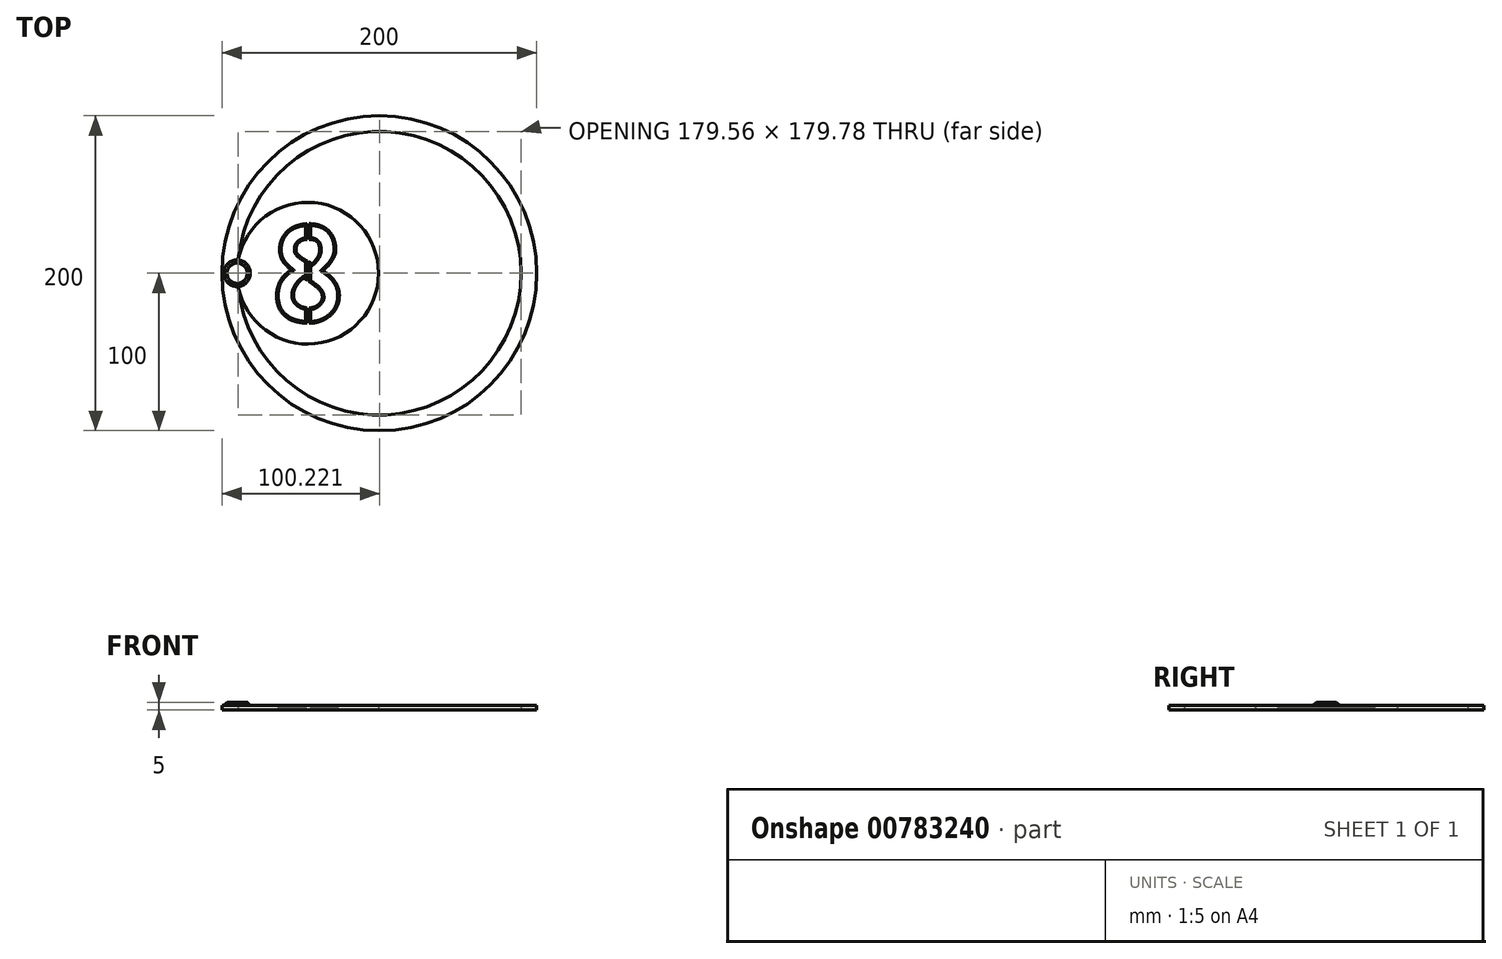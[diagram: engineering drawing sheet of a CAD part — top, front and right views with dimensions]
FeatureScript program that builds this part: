
annotation { "Feature Type Name" : "Feature", "Feature Type Description" : "" }
export const myFeature = defineFeature(function(context is Context, id is Id, definition is map)
    precondition{}
    {
        {
            var Q0;
            Q0=qCreatedBy(makeId("Top.planeOp"),FACE);
            var sketch = newSketch(context, id + "F0", { "sketchPlane" : qUnion([Q0])});
            skCircle(sketch, "E0", {"center": v(0, 0) * mm, "radius": 100 * mm});
            skArc(sketch, "E1", {"start": v(-89.56, -8.9) * mm, "mid": v(90, 0) * mm, "end": v(-89.56, 8.9) * mm});
            skArc(sketch, "E2", {"start": v(-89.56, -8.9) * mm, "mid": v(-0.45, 0) * mm, "end": v(-89.56, 8.9) * mm});
            skText(sketch, "E3", { "text": "8", "fontName": "AllertaStencil-Regular.ttf"});
            const initialGuessF0  = {"E3": [-0.07008, -0.03, 1, 0, 0.06]};
            skSetInitialGuess(sketch, initialGuessF0);
            skSolve(sketch);
        }
        {
            var Q0;
            Q0=makeQuery(id+"F0.imprint","IMPRINT",FACE,{"disambiguationData":[TD([[makeQuery(id+"F0.imprint","IMPRINT",EDGE,{"derivedFrom":sQuery(id+"F0.wireOp",EDGE,"E0")}),1.0]])]});
            extrude(context, id + "F1", {"entities" : qUnion([Q0]), "depth" : 3 * mm, "offsetDistance" : 25 * mm});
        }
        {
            var Q0;
            Q0=makeQuery(id+"F1.opExtrude","CAP_FACE",FACE,{"disambiguationData":[OSD([sQuery(id+"F0.wireOp",EDGE,"E0"),sQuery(id+"F0.wireOp",EDGE,"E1"),sQuery(id+"F0.wireOp",EDGE,"E2"),sQuery(id+"F0.wireOp",EDGE,"E3.sketch_text.stroke-0"),sQuery(id+"F0.wireOp",EDGE,"E3.sketch_text.stroke-1"),sQuery(id+"F0.wireOp",EDGE,"E3.sketch_text.stroke-2"),sQuery(id+"F0.wireOp",EDGE,"E3.sketch_text.stroke-3"),sQuery(id+"F0.wireOp",EDGE,"E3.sketch_text.stroke-4"),sQuery(id+"F0.wireOp",EDGE,"E3.sketch_text.stroke-5"),sQuery(id+"F0.wireOp",EDGE,"E3.sketch_text.stroke-6"),sQuery(id+"F0.wireOp",EDGE,"E3.sketch_text.stroke-7"),sQuery(id+"F0.wireOp",EDGE,"E3.sketch_text.stroke-8"),sQuery(id+"F0.wireOp",EDGE,"E3.sketch_text.stroke-9"),sQuery(id+"F0.wireOp",EDGE,"E3.sketch_text.stroke-10"),sQuery(id+"F0.wireOp",EDGE,"E3.sketch_text.stroke-11"),sQuery(id+"F0.wireOp",EDGE,"E3.sketch_text.stroke-12"),sQuery(id+"F0.wireOp",EDGE,"E3.sketch_text.stroke-13"),sQuery(id+"F0.wireOp",EDGE,"E3.sketch_text.stroke-14"),sQuery(id+"F0.wireOp",EDGE,"E3.sketch_text.stroke-15"),sQuery(id+"F0.wireOp",EDGE,"E3.sketch_text.stroke-16"),sQuery(id+"F0.wireOp",EDGE,"E3.sketch_text.stroke-17"),sQuery(id+"F0.wireOp",EDGE,"E3.sketch_text.stroke-18"),sQuery(id+"F0.wireOp",EDGE,"E3.sketch_text.stroke-19"),sQuery(id+"F0.wireOp",EDGE,"E3.sketch_text.stroke-20"),sQuery(id+"F0.wireOp",EDGE,"E3.sketch_text.stroke-21"),sQuery(id+"F0.wireOp",EDGE,"E3.sketch_text.stroke-22"),sQuery(id+"F0.wireOp",EDGE,"E3.sketch_text.stroke-23"),sQuery(id+"F0.wireOp",EDGE,"E3.sketch_text.stroke-24"),sQuery(id+"F0.wireOp",EDGE,"E3.sketch_text.stroke-25"),sQuery(id+"F0.wireOp",EDGE,"E3.sketch_text.stroke-26"),sQuery(id+"F0.wireOp",EDGE,"E3.sketch_text.stroke-27"),sQuery(id+"F0.wireOp",EDGE,"E3.sketch_text.stroke-28"),sQuery(id+"F0.wireOp",EDGE,"E3.sketch_text.stroke-29"),sQuery(id+"F0.wireOp",EDGE,"E3.sketch_text.stroke-30"),sQuery(id+"F0.wireOp",EDGE,"E3.sketch_text.stroke-31"),sQuery(id+"F0.wireOp",EDGE,"E3.sketch_text.stroke-32"),sQuery(id+"F0.wireOp",EDGE,"E3.sketch_text.stroke-33"),sQuery(id+"F0.wireOp",EDGE,"E3.sketch_text.stroke-34"),sQuery(id+"F0.wireOp",EDGE,"E3.sketch_text.stroke-35"),sQuery(id+"F0.wireOp",EDGE,"E3.sketch_text.stroke-36"),sQuery(id+"F0.wireOp",EDGE,"E3.sketch_text.stroke-37"),sQuery(id+"F0.wireOp",EDGE,"E3.sketch_text.stroke-38"),sQuery(id+"F0.wireOp",EDGE,"E3.sketch_text.stroke-39"),sQuery(id+"F0.wireOp",EDGE,"E3.sketch_text.stroke-40"),sQuery(id+"F0.wireOp",EDGE,"E3.sketch_text.stroke-41"),sQuery(id+"F0.wireOp",EDGE,"E3.sketch_text.stroke-42"),sQuery(id+"F0.wireOp",EDGE,"E3.sketch_text.stroke-43"),sQuery(id+"F0.wireOp",EDGE,"E3.sketch_text.stroke-44"),sQuery(id+"F0.wireOp",EDGE,"E3.sketch_text.stroke-45"),sQuery(id+"F0.wireOp",EDGE,"E3.sketch_text.stroke-46"),sQuery(id+"F0.wireOp",EDGE,"E3.sketch_text.stroke-47"),sQuery(id+"F0.wireOp",EDGE,"E3.sketch_text.stroke-48"),sQuery(id+"F0.wireOp",EDGE,"E3.sketch_text.stroke-49"),sQuery(id+"F0.wireOp",EDGE,"E3.sketch_text.stroke-50"),sQuery(id+"F0.wireOp",EDGE,"E3.sketch_text.stroke-51"),sQuery(id+"F0.wireOp",EDGE,"E3.sketch_text.stroke-52"),sQuery(id+"F0.wireOp",EDGE,"E3.sketch_text.stroke-53")])],"isStart":false});
            var sketch = newSketch(context, id + "F2", { "sketchPlane" : qUnion([Q0])});
            skCircle(sketch, "E4", {"center": v(-90.34, 0) * mm, "radius": 8.44 * mm});
            skSolve(sketch);
        }
        {
            var Q0;
            Q0=makeQuery(id+"F2.imprint","IMPRINT",FACE,{"disambiguationData":[TD([[makeQuery(id+"F2.imprint","IMPRINT",EDGE,{"derivedFrom":sQuery(id+"F2.wireOp",EDGE,"JcdNsVjm-nB0P-Op7M-ulTK-ir5An5YM1DP8")}),1.0]])]});
            var Q1;
            Q1=makeQuery(id+"F2.imprint","IMPRINT",FACE,{"disambiguationData":[TD([[makeQuery(id+"F2.imprint","IMPRINT",EDGE,{"derivedFrom":sQuery(id+"F2.wireOp",EDGE,"E4")}),1.0]])]});
            extrude(context, id + "F3", {"entities" : qUnion([Q0, Q1]), "operationType" : NewBodyOperationType.ADD, "depth" : 2 * mm, "offsetDistance" : 25 * mm});
        }
        {
            var Q0;
            Q0=makeQuery(id+"F3.opExtrude","CAP_EDGE",EDGE,{"disambiguationData":[OSD([sQuery(id+"F2.wireOp",EDGE,"E4")])],"isStart":false});
            chamfer(context, id + "F4", {"entities" : qUnion([Q0]), "width" : 2 * mm, "tangentPropagation" : true});
        }
        {
            var Q0;
            Q0=makeQuery(id+"F1.opExtrude","CAP_EDGE",EDGE,{"disambiguationData":[OSD([sQuery(id+"F0.wireOp",EDGE,"E3.sketch_text.stroke-20")])],"isStart":false});
            var Q1;
            Q1=makeQuery(id+"F1.opExtrude","CAP_EDGE",EDGE,{"disambiguationData":[OSD([sQuery(id+"F0.wireOp",EDGE,"E3.sketch_text.stroke-0")])],"isStart":false});
            var Q2;
            Q2=makeQuery(id+"F1.opExtrude","CAP_EDGE",EDGE,{"disambiguationData":[OSD([sQuery(id+"F0.wireOp",EDGE,"E3.sketch_text.stroke-29")])],"isStart":false});
            var Q3;
            Q3=makeQuery(id+"F1.opExtrude","CAP_EDGE",EDGE,{"disambiguationData":[OSD([sQuery(id+"F0.wireOp",EDGE,"E3.sketch_text.stroke-32")])],"isStart":false});
            var Q4;
            Q4=makeQuery(id+"F1.opExtrude","CAP_EDGE",EDGE,{"disambiguationData":[OSD([sQuery(id+"F0.wireOp",EDGE,"E3.sketch_text.stroke-17")])],"isStart":false});
            var Q5;
            Q5=makeQuery(id+"F1.opExtrude","CAP_EDGE",EDGE,{"disambiguationData":[OSD([sQuery(id+"F0.wireOp",EDGE,"E3.sketch_text.stroke-13")])],"isStart":false});
            var Q6;
            Q6=makeQuery(id+"F1.opExtrude","CAP_EDGE",EDGE,{"disambiguationData":[OSD([sQuery(id+"F0.wireOp",EDGE,"E3.sketch_text.stroke-38")])],"isStart":false});
            var Q7;
            Q7=makeQuery(id+"F1.opExtrude","CAP_EDGE",EDGE,{"disambiguationData":[OSD([sQuery(id+"F0.wireOp",EDGE,"E3.sketch_text.stroke-9")])],"isStart":false});
            var Q8;
            Q8=makeQuery(id+"F1.opExtrude","CAP_EDGE",EDGE,{"disambiguationData":[OSD([sQuery(id+"F0.wireOp",EDGE,"E3.sketch_text.stroke-7")])],"isStart":false});
            var Q9;
            Q9=makeQuery(id+"F1.opExtrude","CAP_EDGE",EDGE,{"disambiguationData":[OSD([sQuery(id+"F0.wireOp",EDGE,"E3.sketch_text.stroke-4")])],"isStart":false});
            var Q10;
            Q10=makeQuery(id+"F1.opExtrude","CAP_EDGE",EDGE,{"disambiguationData":[OSD([sQuery(id+"F0.wireOp",EDGE,"E3.sketch_text.stroke-45")])],"isStart":false});
            var Q11;
            Q11=makeQuery(id+"F1.opExtrude","CAP_EDGE",EDGE,{"disambiguationData":[OSD([sQuery(id+"F0.wireOp",EDGE,"E3.sketch_text.stroke-49")])],"isStart":false});
            var Q12;
            Q12=makeQuery(id+"F1.opExtrude","CAP_EDGE",EDGE,{"disambiguationData":[OSD([sQuery(id+"F0.wireOp",EDGE,"E3.sketch_text.stroke-39")])],"isStart":false});
            var Q13;
            Q13=makeQuery(id+"F1.opExtrude","CAP_EDGE",EDGE,{"disambiguationData":[OSD([sQuery(id+"F0.wireOp",EDGE,"E3.sketch_text.stroke-42")])],"isStart":false});
            var Q14;
            Q14=makeQuery(id+"F1.opExtrude","CAP_EDGE",EDGE,{"disambiguationData":[OSD([sQuery(id+"F0.wireOp",EDGE,"E3.sketch_text.stroke-10")])],"isStart":false});
            var Q15;
            Q15=makeQuery(id+"F1.opExtrude","CAP_EDGE",EDGE,{"disambiguationData":[OSD([sQuery(id+"F0.wireOp",EDGE,"E3.sketch_text.stroke-40")])],"isStart":false});
            chamfer(context, id + "F5", {"entities" : qUnion([Q0, Q1, Q2, Q3, Q4, Q5, Q6, Q7, Q8, Q9, Q10, Q11, Q12, Q13, Q14, Q15]), "width" : 1 * mm, "tangentPropagation" : true});
        }
    });
